# Revit family: Glass Flush Plate
name_source: partatom
category: Plumbing Fixtures
units: mm (PartAtom-declared; Revit-internal decimal feet)

## family parameters
Always vertical = Yes
Cut with Voids When Loaded = No
Enable Cutting in Views = No
Maintain Annotation Orientation = No
OmniClass Number = 23.45.00.00
OmniClass Title = Sanitary, Laundry, and Cleaning Equipment
Part Type = Normal
Room Calculation Point = No
Round Connector Dimension = Use Diameter
Shared = No
Work Plane-Based = No

## types (3) — shared parameters
Category = Concealed Cistern
Fixing Details = https://www.lecicosa.co.za
Manufacturer = Lecico SA
Material = Glass
Model = Glass Flush Plate Only
Technical Dimensions = W248 x H168 x D14mm
URL = https://www.lecicosa.co.za
zero-valued in all types: Default Elevation

## per-type parameters (varying)
| type | Colour | Glass Colour | Product Code |
| Glass Flush Plate - Red | Red | Red Glass | LECFLUGLASREDBC |
| Glass Flush Plate - Black | Black | Black Glass | LECFLUGLASBLABC |
| Glass Flush Plate - White | White | White Glass | LECFLUGLASWHIBC |

## geometry (parser evidence)
native form markers: Sweep x3
no freeform markers — native parametric forms only
